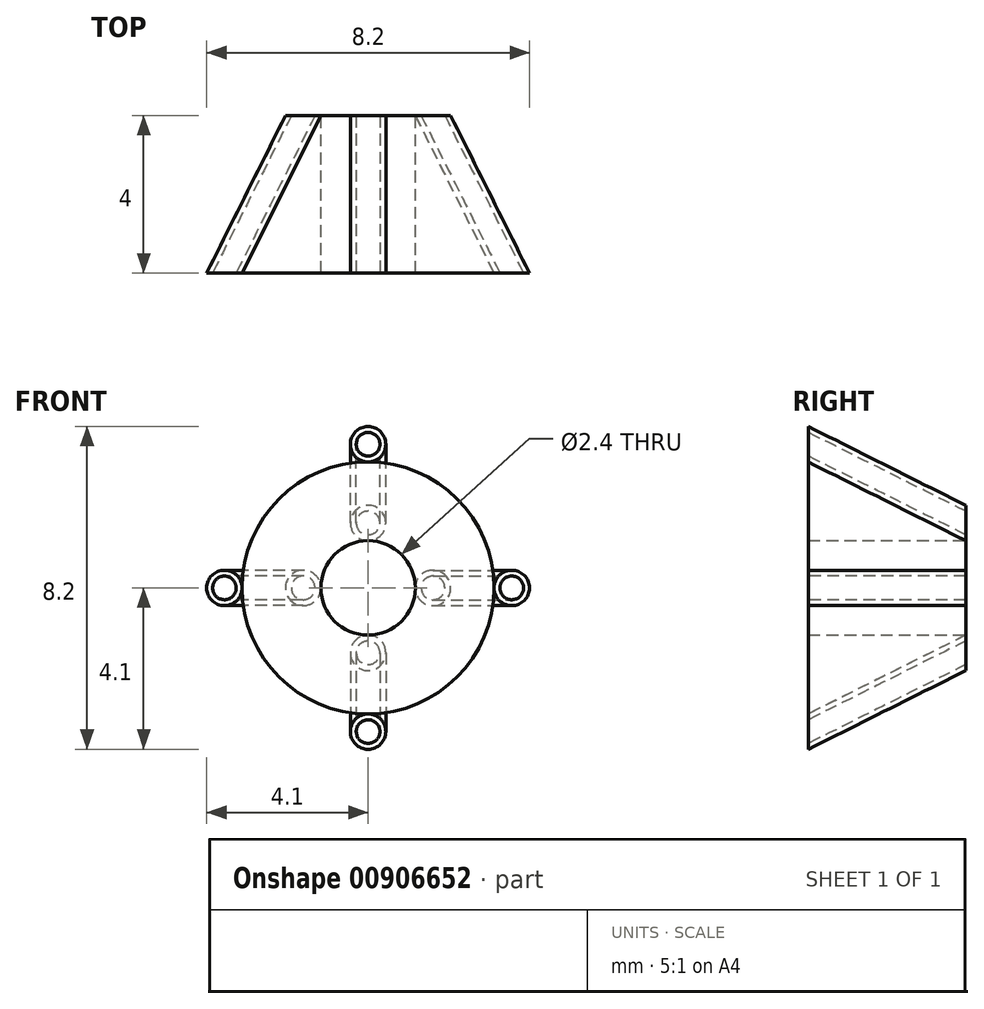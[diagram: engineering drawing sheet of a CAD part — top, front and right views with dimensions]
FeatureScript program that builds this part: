
annotation { "Feature Type Name" : "Feature", "Feature Type Description" : "" }
export const myFeature = defineFeature(function(context is Context, id is Id, definition is map)
    precondition{}
    {
        {
            var Q0;
            Q0=qCreatedBy(makeId("Top.planeOp"),FACE);
            var sketch = newSketch(context, id + "F0", { "sketchPlane" : qUnion([Q0])});
            skLineSegment(sketch, "E0", {"start": v(-1.2, 0) * mm, "end": v(-1.2, 4) * mm});
            skLineSegment(sketch, "E1", {"start": v(-1.2, 4) * mm, "end": v(-3.2, 0) * mm});
            skLineSegment(sketch, "E2", {"start": v(-3.2, 0) * mm, "end": v(-1.2, 0) * mm});
            skLineSegment(sketch, "E3", {"start": v(-1.2, 4) * mm, "end": v(0, 4) * mm});
            skLineSegment(sketch, "E4", {"start": v(0, 4) * mm, "end": v(0, 0) * mm});
            skLineSegment(sketch, "E5", {"start": v(0, 0) * mm, "end": v(-1.2, 0) * mm});
            skSolve(sketch);
        }
        {
            var Q0;
            Q0=makeQuery(id+"F0.imprint","IMPRINT",FACE,{"disambiguationData":[TD([[makeQuery(id+"F0.imprint","IMPRINT",EDGE,{"derivedFrom":sQuery(id+"F0.wireOp",EDGE,"E0")}),1.0]])]});
            var Q1;
            Q1=sQuery(id+"F0.wireOp",EDGE,"E4");
            revolve(context, id + "F1", {"surfaceOperationType" : NewSurfaceOperationType.NEW, "entities" : qUnion([Q0]), "axis" : qUnion([Q1]), "revolveType" : RevolveType.FULL});
        }
        {
            var Q0;
            Q0=sQuery(id+"F0.wireOp",EDGE,"E0");
            cPoint(context, id + "F2", {"entities" : qUnion([Q0]), "parameter" : 0.5});
        }
        {
            var Q0;
            Q0 = qCreatedBy(id + "F2" ,VERTEX);
            var Q1;
            Q1=makeQuery(id+"F1.opRevolve","SWEPT_EDGE",EDGE,{"disambiguationData":[OSD([sQuery(id+"F0.wireOp",EDGE,"E1"),sQuery(id+"F0.wireOp",EDGE,"E2")])]});
            cPlane(context, id + "F3", {"entities" : qUnion([Q0, Q1]), "cplaneType" : CPlaneType.LINE_ANGLE, "offset" : 25 * mm, "angle" : 0 * degree, "width" : 150 * mm, "height" : 150 * mm});
        }
        {
            var Q0;
            Q0=qCreatedBy(id+"F3.planeOp",FACE);
            var sketch = newSketch(context, id + "F4", { "sketchPlane" : qUnion([Q0])});
            skLineSegment(sketch, "E6", {"start": v(-3.2, 0) * mm, "end": v(-1.2, 4) * mm});
            skLineSegment(sketch, "E7", {"start": v(-4.1, 0) * mm, "end": v(-2.1, 4) * mm});
            skLineSegment(sketch, "E8", {"start": v(-2.1, 4) * mm, "end": v(-1.2, 4) * mm});
            skLineSegment(sketch, "E9", {"start": v(-3.2, 0) * mm, "end": v(-4.1, 0) * mm});
            skSolve(sketch);
        }
        {
            var Q0;
            Q0=sQuery(id+"F4.wireOp",EDGE,"E9");
            cPlane(context, id + "F5", {"entities" : qUnion([Q0]), "cplaneType" : CPlaneType.LINE_ANGLE, "offset" : 25 * mm, "angle" : 0 * degree, "width" : 150 * mm, "height" : 150 * mm});
        }
        {
            var Q0;
            Q0=qCreatedBy(id+"F5.planeOp",FACE);
            var sketch = newSketch(context, id + "F6", { "sketchPlane" : qUnion([Q0])});
            skCircle(sketch, "E10", {"center": v(-3.65, 0) * mm, "radius": 0.45 * mm});
            skSolve(sketch);
        }
        {
            var Q0;
            Q0=makeQuery(id+"F6.imprint","IMPRINT",FACE,{"disambiguationData":[TD([[makeQuery(id+"F6.imprint","IMPRINT",EDGE,{"derivedFrom":sQuery(id+"F6.wireOp",EDGE,"E10")}),1.0]])]});
            var Q1;
            Q1=sQuery(id+"F4.wireOp",EDGE,"E6");
            sweep(context, id + "F7", {"profiles" : qUnion([Q0]), "path" : qUnion([Q1])});
        }
        {
            var Q0;
            Q0=makeQuery(id+"F7.opSweep","CAP_FACE",FACE,{"disambiguationData":[OSD([sQuery(id+"F4.wireOp",VERTEX,"E6.start"),sQuery(id+"F6.wireOp",EDGE,"E10")])],"isStart":true});
            var sketch = newSketch(context, id + "F8", { "sketchPlane" : qUnion([Q0])});
            skCircle(sketch, "E11", {"center": v(-3.65, 0) * mm, "radius": 0.3 * mm});
            skSolve(sketch);
        }
        {
            var Q0;
            Q0=makeQuery(id+"F8.imprint","IMPRINT",FACE,{"disambiguationData":[TD([[makeQuery(id+"F8.imprint","IMPRINT",EDGE,{"derivedFrom":sQuery(id+"F8.wireOp",EDGE,"E11")}),1.0]])]});
            var Q1;
            Q1=sQuery(id+"F0.wireOp",EDGE,"E1");
            sweep(context, id + "F9", {"operationType" : NewBodyOperationType.REMOVE, "profiles" : qUnion([Q0]), "path" : qUnion([Q1])});
        }
        {
            var Q0;
            Q0=makeQuery(id+"F7.opSweep","SWEPT_BODY",BODY,{"disambiguationData":[OSD([sQuery(id+"F4.wireOp",EDGE,"E6"),sQuery(id+"F6.wireOp",EDGE,"E10")])]});
            var Q1;
            Q1=makeQuery(id+"F1.opRevolve","SWEPT_EDGE",EDGE,{"disambiguationData":[OSD([sQuery(id+"F0.wireOp",EDGE,"E1"),sQuery(id+"F0.wireOp",EDGE,"E2")])]});
            circularPattern(context, id + "F10", {"entities" : qUnion([Q0]), "axis" : qUnion([Q1]), "angle" : 360 * degree, "instanceCount" : 4, "equalSpace" : true});
        }
    });
